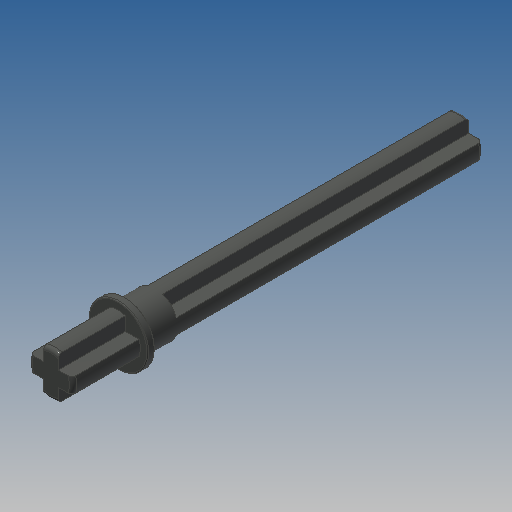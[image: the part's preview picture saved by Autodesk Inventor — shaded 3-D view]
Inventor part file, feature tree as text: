
AUTODESK INVENTOR PART (.ipt)
format: ipt  version: 2022.2 (Build 262287000, 287)  size: 193,024 bytes
history: native  units: in
note: dims shown in document units (in); Inventor stores cm internally (conversion verified against a paired STEP export)
features: extrude x3, sketch x2, plane x1, fillet x1
ambient origin geometry x8: Origin, YZ Plane, XZ Plane, XY Plane, X Axis, Y Axis, Z Axis, Center Point
bodies: Solid1 (feature_tree)
feature tree (7):
  extrude  "Extrusion1"  Depth=0.063in
  plane  "Work Plane1"
  sketch  "Sketch2"  dims[d2=1.7323in d3=0.0in d4=0.0157in d5=0.0in d6=0.0in d7=-0.315in d8=0.252in d9=0.0315in d10=0.0in d11=0.126in d12=0.0in d13=0.0in d14=0.0039in]
  extrude  "Extrusion2"  TaperAngle=0.0deg  [1 undecoded]
  extrude  "Extrusion3"  Depth=0.0157in
  fillet  "Fillet1"  [1 undecoded]
  sketch  "Sketch1"  dims[d0=0.189in d1=0.063in]
note: 2 required parameter values undecoded (feature->parameter linkage not recoverable at this tier; creation-order binding heuristic only, values carry confidence <= 0.55)
